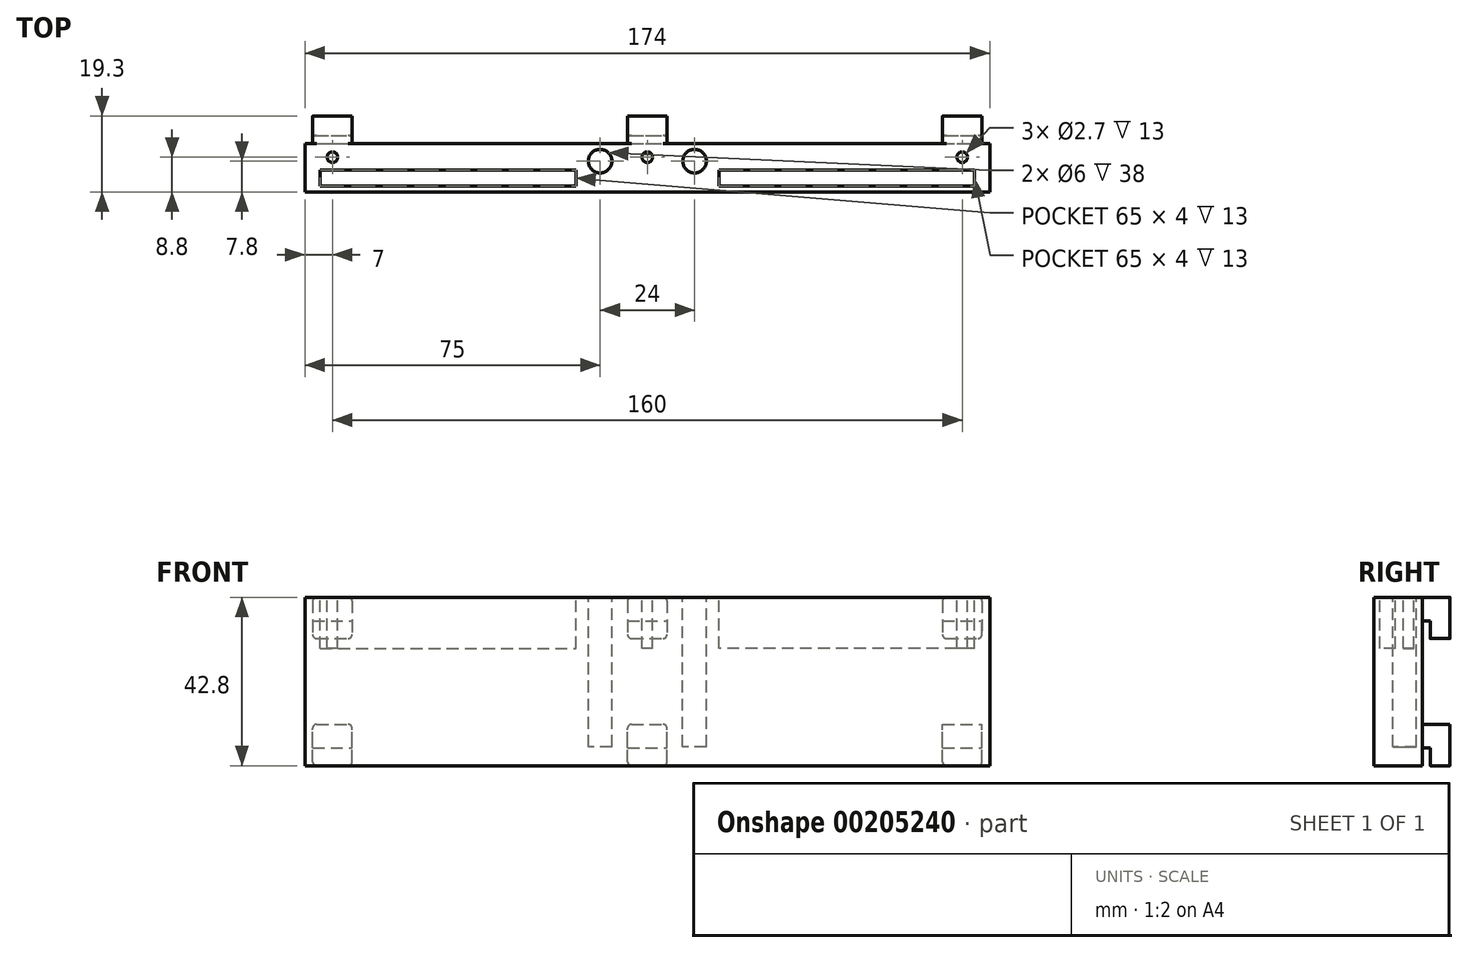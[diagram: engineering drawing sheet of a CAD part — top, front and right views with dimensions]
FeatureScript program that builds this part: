
annotation { "Feature Type Name" : "Feature", "Feature Type Description" : "" }
export const myFeature = defineFeature(function(context is Context, id is Id, definition is map)
    precondition{}
    {
        {
            var Q0;
            Q0=qCreatedBy(makeId("Top.planeOp"),FACE);
            var sketch = newSketch(context, id + "F0", { "sketchPlane" : qUnion([Q0])});
            skLineSegment(sketch, "E0.bottom", {"start": v(-87, 0) * mm, "end": v(87, 0) * mm});
            skLineSegment(sketch, "E0.top", {"start": v(-87, -12.3) * mm, "end": v(87, -12.3) * mm});
            skLineSegment(sketch, "E0.left", {"start": v(-87, 0) * mm, "end": v(-87, -12.3) * mm});
            skLineSegment(sketch, "E0.right", {"start": v(87, 0) * mm, "end": v(87, -12.3) * mm});
            skSolve(sketch);
        }
        {
            var Q0;
            Q0 = qSketchRegion(id + "F0", true);
            extrude(context, id + "F1", {"entities" : qUnion([Q0]), "depth" : 42.8 * mm});
        }
        {
            var Q0;
            Q0=makeQuery(id+"F1.opExtrude","SWEPT_FACE",FACE,{"disambiguationData":[OSD([sQuery(id+"F0.wireOp",EDGE,"E0.bottom")])]});
            var sketch = newSketch(context, id + "F2", { "sketchPlane" : qUnion([Q0])});
            skLineSegment(sketch, "E1.bottom", {"start": v(85, 42.8) * mm, "end": v(75, 42.8) * mm});
            skLineSegment(sketch, "E1.top", {"start": v(85, 32.3) * mm, "end": v(75, 32.3) * mm});
            skLineSegment(sketch, "E1.left", {"start": v(85, 42.8) * mm, "end": v(85, 32.3) * mm});
            skLineSegment(sketch, "E1.right", {"start": v(75, 42.8) * mm, "end": v(75, 32.3) * mm});
            skLineSegment(sketch, "E2.bottom", {"start": v(5, 42.8) * mm, "end": v(-5, 42.8) * mm});
            skLineSegment(sketch, "E2.top", {"start": v(5, 32.3) * mm, "end": v(-5, 32.3) * mm});
            skLineSegment(sketch, "E2.left", {"start": v(5, 42.8) * mm, "end": v(5, 32.3) * mm});
            skLineSegment(sketch, "E2.right", {"start": v(-5, 42.8) * mm, "end": v(-5, 32.3) * mm});
            skLineSegment(sketch, "E3.bottom", {"start": v(-75, 42.8) * mm, "end": v(-85, 42.8) * mm});
            skLineSegment(sketch, "E3.top", {"start": v(-75, 32.3) * mm, "end": v(-85, 32.3) * mm});
            skLineSegment(sketch, "E3.left", {"start": v(-75, 42.8) * mm, "end": v(-75, 32.3) * mm});
            skLineSegment(sketch, "E3.right", {"start": v(-85, 42.8) * mm, "end": v(-85, 32.3) * mm});
            skLineSegment(sketch, "E4", {"start": v(80, 61.51) * mm, "end": v(80, -18.94) * mm, "construction": true});
            skLineSegment(sketch, "E5", {"start": v(-80, 62.73) * mm, "end": v(-80, -15.92) * mm, "construction": true});
            skLineSegment(sketch, "E6", {"start": v(106.4, 21.4) * mm, "end": v(-110.47, 21.4) * mm, "construction": true});
            skPoint(sketch, "E6.startSnap0", {"position": v(87, 21.4) * mm});
            skPoint(sketch, "E6.endSnap0", {"position": v(-87, 21.4) * mm});
            skLineSegment(sketch, "E7.MirrorCS", {"start": v(85, 0) * mm, "end": v(75, 0) * mm});
            skLineSegment(sketch, "E8.MirrorCS", {"start": v(85, 0) * mm, "end": v(85, 10.5) * mm});
            skLineSegment(sketch, "E9.MirrorCS", {"start": v(85, 10.5) * mm, "end": v(75, 10.5) * mm});
            skLineSegment(sketch, "E10.MirrorCS", {"start": v(75, 0) * mm, "end": v(75, 10.5) * mm});
            skLineSegment(sketch, "E11.MirrorCS", {"start": v(5, 0) * mm, "end": v(5, 10.5) * mm});
            skLineSegment(sketch, "E12.MirrorCS", {"start": v(5, 0) * mm, "end": v(-5, 0) * mm});
            skLineSegment(sketch, "E13.MirrorCS", {"start": v(5, 10.5) * mm, "end": v(-5, 10.5) * mm});
            skLineSegment(sketch, "E14.MirrorCS", {"start": v(-5, 0) * mm, "end": v(-5, 10.5) * mm});
            skLineSegment(sketch, "E15.MirrorCS", {"start": v(-75, 0) * mm, "end": v(-85, 0) * mm});
            skLineSegment(sketch, "E16.MirrorCS", {"start": v(-75, 0) * mm, "end": v(-75, 10.5) * mm});
            skLineSegment(sketch, "E17.MirrorCS", {"start": v(-75, 10.5) * mm, "end": v(-85, 10.5) * mm});
            skLineSegment(sketch, "E18.MirrorCS", {"start": v(-85, 0) * mm, "end": v(-85, 10.5) * mm});
            skLineSegment(sketch, "E19.bottom", {"start": v(5, 26.65) * mm, "end": v(-5, 26.65) * mm, "construction": true});
            skLineSegment(sketch, "E19.top", {"start": v(5, 16.15) * mm, "end": v(-5, 16.15) * mm, "construction": true});
            skLineSegment(sketch, "E19.left", {"start": v(5, 26.65) * mm, "end": v(5, 16.15) * mm, "construction": true});
            skLineSegment(sketch, "E19.right", {"start": v(-5, 26.65) * mm, "end": v(-5, 16.15) * mm, "construction": true});
            skSolve(sketch);
        }
        {
            var Q0;
            Q0 = qSketchRegion(id + "F2", true);
            extrude(context, id + "F3", {"entities" : qUnion([Q0]), "operationType" : NewBodyOperationType.ADD, "depth" : 7 * mm});
        }
        {
            var Q0;
            Q0=makeQuery(id+"F3.opExtrude","SWEPT_FACE",FACE,{"disambiguationData":[OSD([sQuery(id+"F2.wireOp",EDGE,"E3.right")])]});
            var sketch = newSketch(context, id + "F4", { "sketchPlane" : qUnion([Q0])});
            skLineSegment(sketch, "E20.bottom", {"start": v(0, 32.3) * mm, "end": v(2, 32.3) * mm});
            skLineSegment(sketch, "E20.top", {"start": v(0, 36.8) * mm, "end": v(2, 36.8) * mm});
            skLineSegment(sketch, "E20.left", {"start": v(0, 32.3) * mm, "end": v(0, 36.8) * mm});
            skLineSegment(sketch, "E20.right", {"start": v(2, 32.3) * mm, "end": v(2, 36.8) * mm});
            skLineSegment(sketch, "E21.bottom", {"start": v(0, 0) * mm, "end": v(2, 0) * mm});
            skLineSegment(sketch, "E21.top", {"start": v(0, 4.5) * mm, "end": v(2, 4.5) * mm});
            skLineSegment(sketch, "E21.left", {"start": v(0, 0) * mm, "end": v(0, 4.5) * mm});
            skLineSegment(sketch, "E21.right", {"start": v(2, 0) * mm, "end": v(2, 4.5) * mm});
            skSolve(sketch);
        }
        {
            var Q0;
            Q0 = qSketchRegion(id + "F4", true);
            extrude(context, id + "F5", {"entities" : qUnion([Q0]), "operationType" : NewBodyOperationType.REMOVE, "endBound" : BoundingType.THROUGH_ALL, "oppositeDirection" : true, "depth" : 25 * mm});
        }
        {
            var Q0;
            Q0=makeQuery(id+"F3.boolean.opBoolean","MERGE",FACE,{"derivedFrom":[makeQuery(id+"F1.opExtrude","CAP_FACE",FACE,{"disambiguationData":[OSD([sQuery(id+"F0.wireOp",EDGE,"E0.bottom"),sQuery(id+"F0.wireOp",EDGE,"E0.top"),sQuery(id+"F0.wireOp",EDGE,"E0.left"),sQuery(id+"F0.wireOp",EDGE,"E0.right")])],"isStart":false}),makeQuery(id+"F3.opExtrude","SWEPT_FACE",FACE,{"disambiguationData":[OSD([sQuery(id+"F2.wireOp",EDGE,"E1.bottom")])]}),makeQuery(id+"F3.opExtrude","SWEPT_FACE",FACE,{"disambiguationData":[OSD([sQuery(id+"F2.wireOp",EDGE,"E2.bottom")])]}),makeQuery(id+"F3.opExtrude","SWEPT_FACE",FACE,{"disambiguationData":[OSD([sQuery(id+"F2.wireOp",EDGE,"E3.bottom")])]})]});
            var sketch = newSketch(context, id + "F6", { "sketchPlane" : qUnion([Q0])});
            skLineSegment(sketch, "E22", {"start": v(-50.65, 23.18) * mm, "end": v(-50.65, -34.74) * mm, "construction": true});
            skLineSegment(sketch, "E23", {"start": v(50.65, 23.18) * mm, "end": v(50.65, -38.47) * mm, "construction": true});
            skLineSegment(sketch, "E24.bottom", {"start": v(-83.15, -6.8) * mm, "end": v(-18.15, -6.8) * mm});
            skLineSegment(sketch, "E24.top", {"start": v(-83.15, -10.8) * mm, "end": v(-18.15, -10.8) * mm});
            skLineSegment(sketch, "E24.left", {"start": v(-83.15, -6.8) * mm, "end": v(-83.15, -10.8) * mm});
            skLineSegment(sketch, "E24.right", {"start": v(-18.15, -6.8) * mm, "end": v(-18.15, -10.8) * mm});
            skLineSegment(sketch, "E25.MirrorCS", {"start": v(18.15, -6.8) * mm, "end": v(18.15, -10.8) * mm});
            skLineSegment(sketch, "E26.MirrorCS", {"start": v(83.15, -6.8) * mm, "end": v(18.15, -6.8) * mm});
            skLineSegment(sketch, "E27.MirrorCS", {"start": v(83.15, -6.8) * mm, "end": v(83.15, -10.8) * mm});
            skLineSegment(sketch, "E28.MirrorCS", {"start": v(83.15, -10.8) * mm, "end": v(18.15, -10.8) * mm});
            skLineSegment(sketch, "E29", {"start": v(-91.9, -3.5) * mm, "end": v(99.57, -3.5) * mm, "construction": true});
            skLineSegment(sketch, "E30", {"start": v(80, 14.42) * mm, "end": v(80, -18.6) * mm, "construction": true});
            skPoint(sketch, "E30.startSnap0", {"position": v(80, 7) * mm});
            skLineSegment(sketch, "E31", {"start": v(-80, 14.04) * mm, "end": v(-80, -31.58) * mm, "construction": true});
            skPoint(sketch, "E31.startSnap0", {"position": v(-80, 7) * mm});
            skCircle(sketch, "E32", {"center": v(-80, -3.5) * mm, "radius": 1.35 * mm});
            skCircle(sketch, "E33", {"center": v(0, -3.5) * mm, "radius": 1.35 * mm});
            skCircle(sketch, "E34", {"center": v(80, -3.5) * mm, "radius": 1.35 * mm});
            skSolve(sketch);
        }
        {
            var Q0;
            Q0 = qSketchRegion(id + "F6", true);
            extrude(context, id + "F7", {"entities" : qUnion([Q0]), "operationType" : NewBodyOperationType.REMOVE, "oppositeDirection" : true, "depth" : 13 * mm});
        }
        {
            var Q0;
            Q0=makeQuery(id+"F3.opExtrude","SWEPT_EDGE",EDGE,{"disambiguationData":[OSD([sQuery(id+"F0.wireOp",EDGE,"E0.bottom"),sQuery(id+"F2.wireOp",EDGE,"E2.bottom"),sQuery(id+"F2.wireOp",EDGE,"E2.left")])]});
            var Q1;
            Q1=makeQuery(id+"F3.opExtrude","SWEPT_EDGE",EDGE,{"disambiguationData":[OSD([sQuery(id+"F0.wireOp",EDGE,"E0.bottom"),sQuery(id+"F2.wireOp",EDGE,"E2.bottom"),sQuery(id+"F2.wireOp",EDGE,"E2.right")])]});
            var Q2;
            Q2=makeQuery(id+"F3.opExtrude","SWEPT_EDGE",EDGE,{"disambiguationData":[OSD([sQuery(id+"F0.wireOp",EDGE,"E0.bottom"),sQuery(id+"F2.wireOp",EDGE,"E1.bottom"),sQuery(id+"F2.wireOp",EDGE,"E1.right")])]});
            var Q3;
            Q3=makeQuery(id+"F3.opExtrude","SWEPT_EDGE",EDGE,{"disambiguationData":[OSD([sQuery(id+"F0.wireOp",EDGE,"E0.bottom"),sQuery(id+"F2.wireOp",EDGE,"E1.bottom"),sQuery(id+"F2.wireOp",EDGE,"E1.left")])]});
            var Q4;
            Q4=makeQuery(id+"F3.opExtrude","SWEPT_EDGE",EDGE,{"disambiguationData":[OSD([sQuery(id+"F0.wireOp",EDGE,"E0.bottom"),sQuery(id+"F2.wireOp",EDGE,"E3.bottom"),sQuery(id+"F2.wireOp",EDGE,"E3.left")])]});
            var Q5;
            Q5=makeQuery(id+"F3.opExtrude","SWEPT_EDGE",EDGE,{"disambiguationData":[OSD([sQuery(id+"F0.wireOp",EDGE,"E0.bottom"),sQuery(id+"F2.wireOp",EDGE,"E3.bottom"),sQuery(id+"F2.wireOp",EDGE,"E3.right")])]});
            var Q6;
            Q6=makeQuery(id+"F3.opExtrude","SWEPT_EDGE",EDGE,{"disambiguationData":[OSD([sQuery(id+"F2.wireOp",EDGE,"E13.MirrorCS"),sQuery(id+"F2.wireOp",EDGE,"E14.MirrorCS")])]});
            var Q7;
            Q7=makeQuery(id+"F3.opExtrude","SWEPT_EDGE",EDGE,{"disambiguationData":[OSD([sQuery(id+"F2.wireOp",EDGE,"E11.MirrorCS"),sQuery(id+"F2.wireOp",EDGE,"E13.MirrorCS")])]});
            var Q8;
            Q8=makeQuery(id+"F3.opExtrude","SWEPT_EDGE",EDGE,{"disambiguationData":[OSD([sQuery(id+"F2.wireOp",EDGE,"E9.MirrorCS"),sQuery(id+"F2.wireOp",EDGE,"E10.MirrorCS")])]});
            var Q9;
            Q9=makeQuery(id+"F3.opExtrude","SWEPT_EDGE",EDGE,{"disambiguationData":[OSD([sQuery(id+"F2.wireOp",EDGE,"E8.MirrorCS"),sQuery(id+"F2.wireOp",EDGE,"E9.MirrorCS")])]});
            var Q10;
            Q10=makeQuery(id+"F3.opExtrude","SWEPT_EDGE",EDGE,{"disambiguationData":[OSD([sQuery(id+"F2.wireOp",EDGE,"E3.top"),sQuery(id+"F2.wireOp",EDGE,"E3.right")])]});
            var Q11;
            Q11=makeQuery(id+"F3.opExtrude","SWEPT_EDGE",EDGE,{"disambiguationData":[OSD([sQuery(id+"F0.wireOp",EDGE,"E0.bottom"),sQuery(id+"F2.wireOp",EDGE,"E15.MirrorCS"),sQuery(id+"F2.wireOp",EDGE,"E18.MirrorCS")])]});
            var Q12;
            Q12=makeQuery(id+"F3.opExtrude","SWEPT_EDGE",EDGE,{"disambiguationData":[OSD([sQuery(id+"F0.wireOp",EDGE,"E0.bottom"),sQuery(id+"F2.wireOp",EDGE,"E15.MirrorCS"),sQuery(id+"F2.wireOp",EDGE,"E16.MirrorCS")])]});
            var Q13;
            Q13=makeQuery(id+"F3.opExtrude","SWEPT_EDGE",EDGE,{"disambiguationData":[OSD([sQuery(id+"F2.wireOp",EDGE,"E2.top"),sQuery(id+"F2.wireOp",EDGE,"E2.right")])]});
            var Q14;
            Q14=makeQuery(id+"F3.opExtrude","SWEPT_EDGE",EDGE,{"disambiguationData":[OSD([sQuery(id+"F0.wireOp",EDGE,"E0.bottom"),sQuery(id+"F2.wireOp",EDGE,"E12.MirrorCS"),sQuery(id+"F2.wireOp",EDGE,"E14.MirrorCS")])]});
            var Q15;
            Q15=makeQuery(id+"F3.opExtrude","SWEPT_EDGE",EDGE,{"disambiguationData":[OSD([sQuery(id+"F0.wireOp",EDGE,"E0.bottom"),sQuery(id+"F2.wireOp",EDGE,"E11.MirrorCS"),sQuery(id+"F2.wireOp",EDGE,"E12.MirrorCS")])]});
            var Q16;
            Q16=makeQuery(id+"F3.opExtrude","SWEPT_EDGE",EDGE,{"disambiguationData":[OSD([sQuery(id+"F2.wireOp",EDGE,"E1.top"),sQuery(id+"F2.wireOp",EDGE,"E1.right")])]});
            var Q17;
            Q17=makeQuery(id+"F3.opExtrude","SWEPT_EDGE",EDGE,{"disambiguationData":[OSD([sQuery(id+"F0.wireOp",EDGE,"E0.bottom"),sQuery(id+"F2.wireOp",EDGE,"E7.MirrorCS"),sQuery(id+"F2.wireOp",EDGE,"E10.MirrorCS")])]});
            var Q18;
            Q18=makeQuery(id+"F3.opExtrude","SWEPT_EDGE",EDGE,{"disambiguationData":[OSD([sQuery(id+"F0.wireOp",EDGE,"E0.bottom"),sQuery(id+"F2.wireOp",EDGE,"E7.MirrorCS"),sQuery(id+"F2.wireOp",EDGE,"E8.MirrorCS")])]});
            var Q19;
            Q19=makeQuery(id+"F3.opExtrude","SWEPT_EDGE",EDGE,{"disambiguationData":[OSD([sQuery(id+"F2.wireOp",EDGE,"E1.top"),sQuery(id+"F2.wireOp",EDGE,"E1.left")])]});
            var Q20;
            Q20=makeQuery(id+"F3.opExtrude","SWEPT_EDGE",EDGE,{"disambiguationData":[OSD([sQuery(id+"F2.wireOp",EDGE,"E2.top"),sQuery(id+"F2.wireOp",EDGE,"E2.left")])]});
            var Q21;
            Q21=makeQuery(id+"F3.opExtrude","SWEPT_EDGE",EDGE,{"disambiguationData":[OSD([sQuery(id+"F2.wireOp",EDGE,"E3.top"),sQuery(id+"F2.wireOp",EDGE,"E3.left")])]});
            fillet(context, id + "F8", {"entities" : qUnion([Q0, Q1, Q2, Q3, Q4, Q5, Q6, Q7, Q8, Q9, Q10, Q11, Q12, Q13, Q14, Q15, Q16, Q17, Q18, Q19, Q20, Q21]), "radius" : 1 * mm, "tangentPropagation" : true, "allowEdgeOverflow" : false});
        }
        {
            var Q0;
            Q0=makeQuery(id+"F3.boolean.opBoolean","MERGE",FACE,{"derivedFrom":[makeQuery(id+"F1.opExtrude","CAP_FACE",FACE,{"disambiguationData":[OSD([sQuery(id+"F0.wireOp",EDGE,"E0.bottom"),sQuery(id+"F0.wireOp",EDGE,"E0.top"),sQuery(id+"F0.wireOp",EDGE,"E0.left"),sQuery(id+"F0.wireOp",EDGE,"E0.right")])],"isStart":false}),makeQuery(id+"F3.opExtrude","SWEPT_FACE",FACE,{"disambiguationData":[OSD([sQuery(id+"F2.wireOp",EDGE,"E1.bottom")])]}),makeQuery(id+"F3.opExtrude","SWEPT_FACE",FACE,{"disambiguationData":[OSD([sQuery(id+"F2.wireOp",EDGE,"E2.bottom")])]}),makeQuery(id+"F3.opExtrude","SWEPT_FACE",FACE,{"disambiguationData":[OSD([sQuery(id+"F2.wireOp",EDGE,"E3.bottom")])]})]});
            var sketch = newSketch(context, id + "F9", { "sketchPlane" : qUnion([Q0])});
            skLineSegment(sketch, "E35", {"start": v(126.03, -4.5) * mm, "end": v(-132.49, -4.5) * mm, "construction": true});
            skCircle(sketch, "E36", {"center": v(12, -4.5) * mm, "radius": 3 * mm});
            skCircle(sketch, "E37", {"center": v(-12, -4.5) * mm, "radius": 3 * mm});
            skSolve(sketch);
        }
        {
            var Q0;
            Q0 = qSketchRegion(id + "F9", true);
            extrude(context, id + "F10", {"entities" : qUnion([Q0]), "operationType" : NewBodyOperationType.REMOVE, "oppositeDirection" : true, "depth" : 38 * mm});
        }
    });
